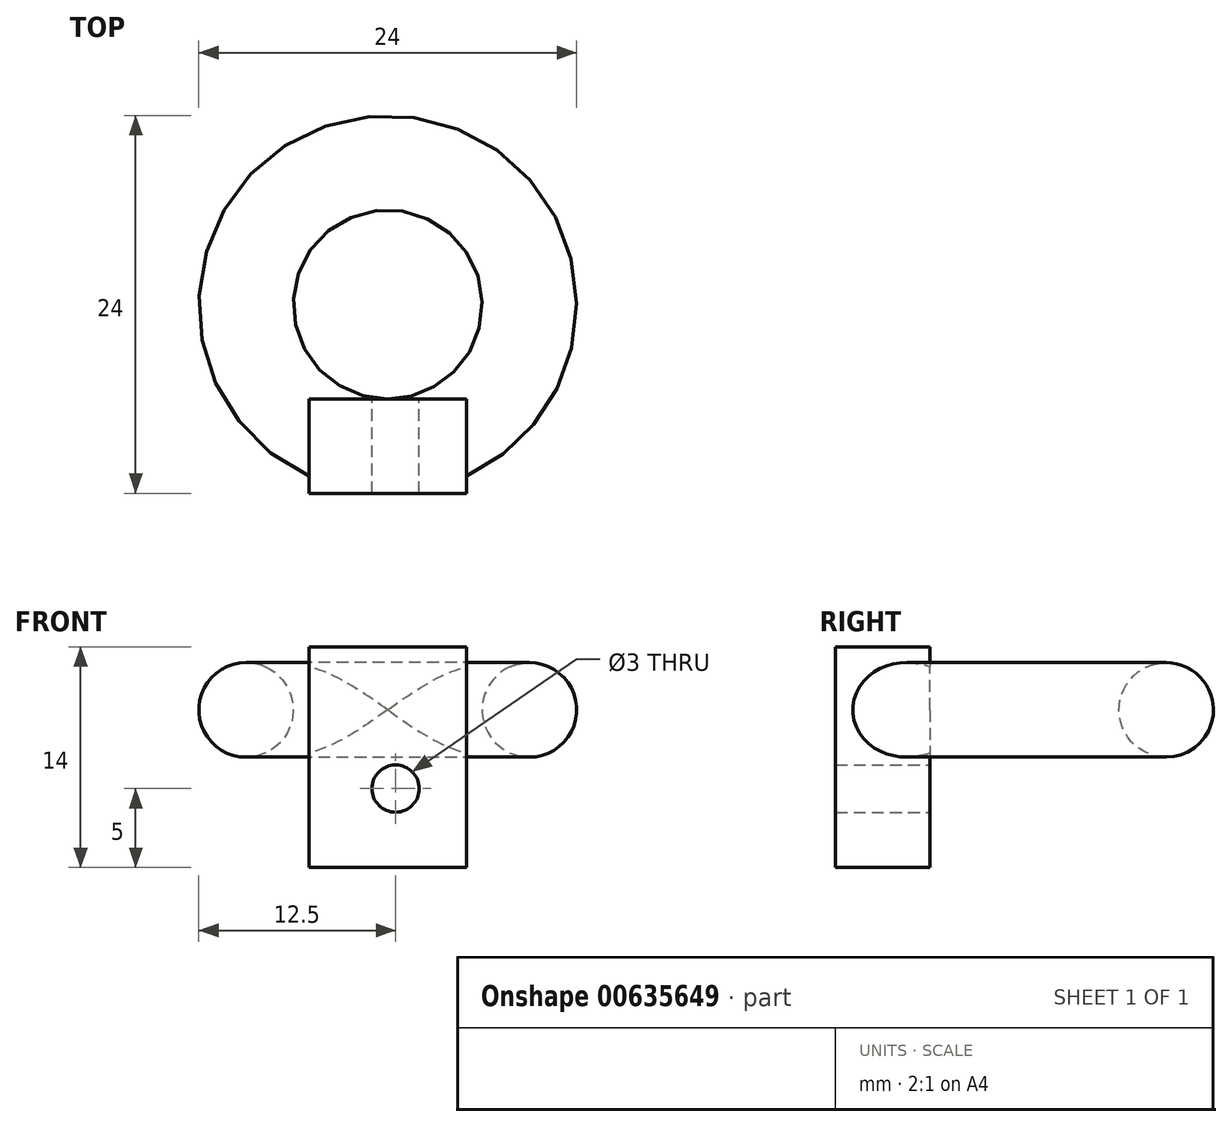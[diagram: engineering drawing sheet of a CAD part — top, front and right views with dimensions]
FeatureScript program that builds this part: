
annotation { "Feature Type Name" : "Feature", "Feature Type Description" : "" }
export const myFeature = defineFeature(function(context is Context, id is Id, definition is map)
    precondition{}
    {
        {
            var Q0;
            Q0=qCreatedBy(makeId("Front.planeOp"),FACE);
            var sketch = newSketch(context, id + "F0", { "sketchPlane" : qUnion([Q0])});
            skLineSegment(sketch, "E0.bottom", {"start": v(-5, 7) * mm, "end": v(5, 7) * mm});
            skLineSegment(sketch, "E0.top", {"start": v(-5, -7) * mm, "end": v(5, -7) * mm});
            skLineSegment(sketch, "E0.left", {"start": v(-5, 7) * mm, "end": v(-5, -7) * mm});
            skLineSegment(sketch, "E0.right", {"start": v(5, 7) * mm, "end": v(5, -7) * mm});
            skSolve(sketch);
        }
        {
            var Q0;
            Q0 = qSketchRegion(id + "F0", true);
            extrude(context, id + "F1", {"entities" : qUnion([Q0]), "oppositeDirection" : true, "depth" : 6 * mm, "offsetDistance" : 25 * mm});
        }
        {
            var Q0;
            Q0=qCreatedBy(makeId("Right.planeOp"),FACE);
            var sketch = newSketch(context, id + "F2", { "sketchPlane" : qUnion([Q0])});
            skCircle(sketch, "E1", {"center": v(3, 3) * mm, "radius": 3 * mm});
            skLineSegment(sketch, "E2", {"start": v(12, 18.47) * mm, "end": v(12, -18.93) * mm, "construction": true});
            skSolve(sketch);
        }
        {
            var Q0;
            Q0 = qSketchRegion(id + "F2", true);
            var Q1;
            Q1=sQuery(id+"F2.wireOp",EDGE,"E2");
            revolve(context, id + "F3", {"operationType" : NewBodyOperationType.ADD, "entities" : qUnion([Q0]), "axis" : qUnion([Q1]), "revolveType" : RevolveType.FULL});
        }
        {
            var Q0;
            {var subQ0=sQuery(id+"F0.wireOp",EDGE,"E0.right");var subQ1=sQuery(id+"F0.wireOp",EDGE,"E0.left");var subQ2=sQuery(id+"F0.wireOp",EDGE,"E0.top");var subQ3=makeQuery(id+"F1.opExtrude","CAP_FACE",FACE,{"disambiguationData":[OSD([sQuery(id+"F0.wireOp",EDGE,"E0.bottom"),subQ2,subQ1,subQ0])],"isStart":false});Q0=makeQuery(id+"F3.boolean.opBoolean","SPLIT",FACE,{"disambiguationData":[TD([makeQuery(id+"F1.opExtrude","SWEPT_FACE",FACE,{"disambiguationData":[OSD([subQ2])]})])],"derivedFrom":subQ3});}
            var sketch = newSketch(context, id + "F4", { "sketchPlane" : qUnion([Q0])});
            skPoint(sketch, "E3", {"position": v(-0.5, -2) * mm});
            skCircle(sketch, "E4", {"center": v(-0.5, -2) * mm, "radius": 1.5 * mm});
            skSolve(sketch);
        }
        {
            var Q0;
            Q0=makeQuery(id+"F4.imprint","IMPRINT",FACE,{"disambiguationData":[TD([[makeQuery(id+"F4.imprint","IMPRINT",EDGE,{"derivedFrom":sQuery(id+"F4.wireOp",EDGE,"E4")}),1.0]])]});
            var Q1;
            Q1=sQuery(id+"F4.wireOp",EDGE,"E4");
            extrude(context, id + "F5", {"entities" : qUnion([Q0]), "operationType" : NewBodyOperationType.REMOVE, "surfaceEntities" : qUnion([Q1]), "endBound" : BoundingType.THROUGH_ALL, "oppositeDirection" : true, "depth" : 25 * mm, "offsetDistance" : 25 * mm});
        }
    });
